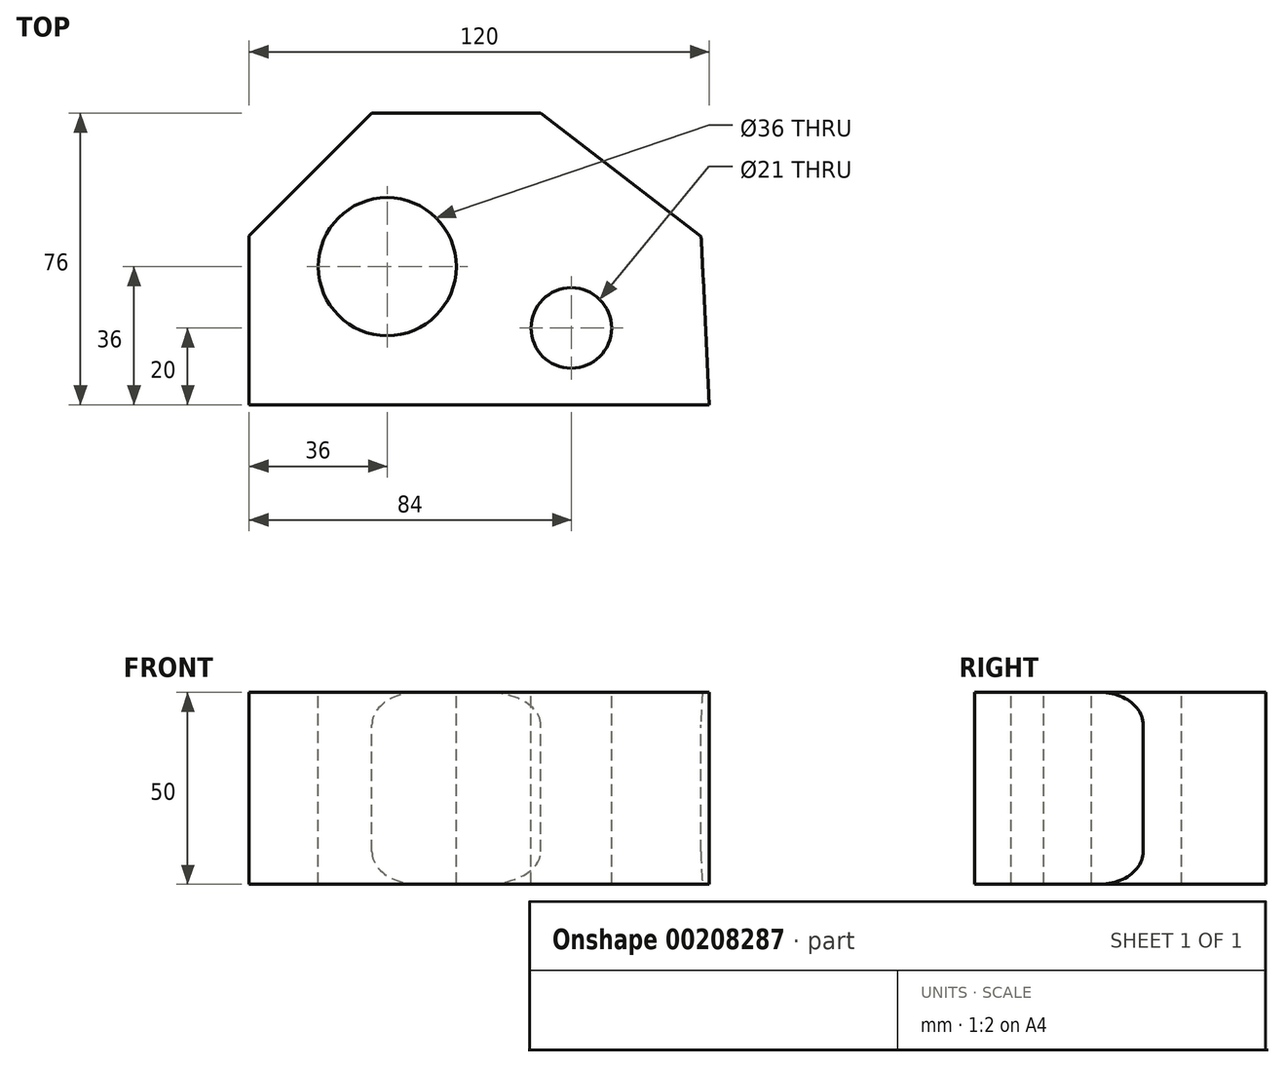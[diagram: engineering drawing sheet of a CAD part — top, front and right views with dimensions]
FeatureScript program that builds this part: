
annotation { "Feature Type Name" : "Feature", "Feature Type Description" : "" }
export const myFeature = defineFeature(function(context is Context, id is Id, definition is map)
    precondition{}
    {
        {
            var Q0;
            Q0=qCreatedBy(makeId("Top.planeOp"),FACE);
            var sketch = newSketch(context, id + "F0", { "sketchPlane" : qUnion([Q0])});
            skLineSegment(sketch, "E0", {"start": v(0, 0) * mm, "end": v(120, 0) * mm});
            skLineSegment(sketch, "E1", {"start": v(0, 0) * mm, "end": v(0, 44) * mm});
            skLineSegment(sketch, "E2", {"start": v(0, 44) * mm, "end": v(32, 76) * mm});
            skLineSegment(sketch, "E3", {"start": v(32, 76) * mm, "end": v(76, 76) * mm});
            skLineSegment(sketch, "E4", {"start": v(76, 76) * mm, "end": v(117.84, 43.95) * mm});
            skLineSegment(sketch, "E5", {"start": v(117.84, 43.95) * mm, "end": v(120, 0) * mm});
            skCircle(sketch, "E6", {"center": v(36, 36) * mm, "radius": 18 * mm});
            skCircle(sketch, "E7", {"center": v(84, 20) * mm, "radius": 10.5 * mm});
            skSolve(sketch);
        }
        {
            var Q0;
            Q0=makeQuery(id+"F0.imprint","IMPRINT",FACE,{"disambiguationData":[TD([[makeQuery(id+"F0.imprint","IMPRINT",EDGE,{"derivedFrom":sQuery(id+"F0.wireOp",EDGE,"E0")}),1.0]])]});
            extrude(context, id + "F1", {"entities" : qUnion([Q0]), "oppositeDirection" : true, "depth" : 50 * mm});
        }
        {
            var Q0;
            Q0=makeQuery(id+"F1.opExtrude","CAP_EDGE",EDGE,{"disambiguationData":[OSD([sQuery(id+"F0.wireOp",EDGE,"E4")])],"isStart":true});
            var Q1;
            Q1=makeQuery(id+"F1.opExtrude","CAP_EDGE",EDGE,{"disambiguationData":[OSD([sQuery(id+"F0.wireOp",EDGE,"E4")])],"isStart":false});
            fillet(context, id + "F2", {"entities" : qUnion([Q0, Q1]), "radius" : 8.5 * mm, "tangentPropagation" : true, "allowEdgeOverflow" : false});
        }
        {
            var Q0;
            Q0=makeQuery(id+"F1.opExtrude","CAP_EDGE",EDGE,{"disambiguationData":[OSD([sQuery(id+"F0.wireOp",EDGE,"E2")])],"isStart":true});
            var Q1;
            Q1=makeQuery(id+"F1.opExtrude","CAP_EDGE",EDGE,{"disambiguationData":[OSD([sQuery(id+"F0.wireOp",EDGE,"E2")])],"isStart":false});
            fillet(context, id + "F3", {"entities" : qUnion([Q0, Q1]), "radius" : 8.5 * mm, "tangentPropagation" : true, "allowEdgeOverflow" : false});
        }
    });
